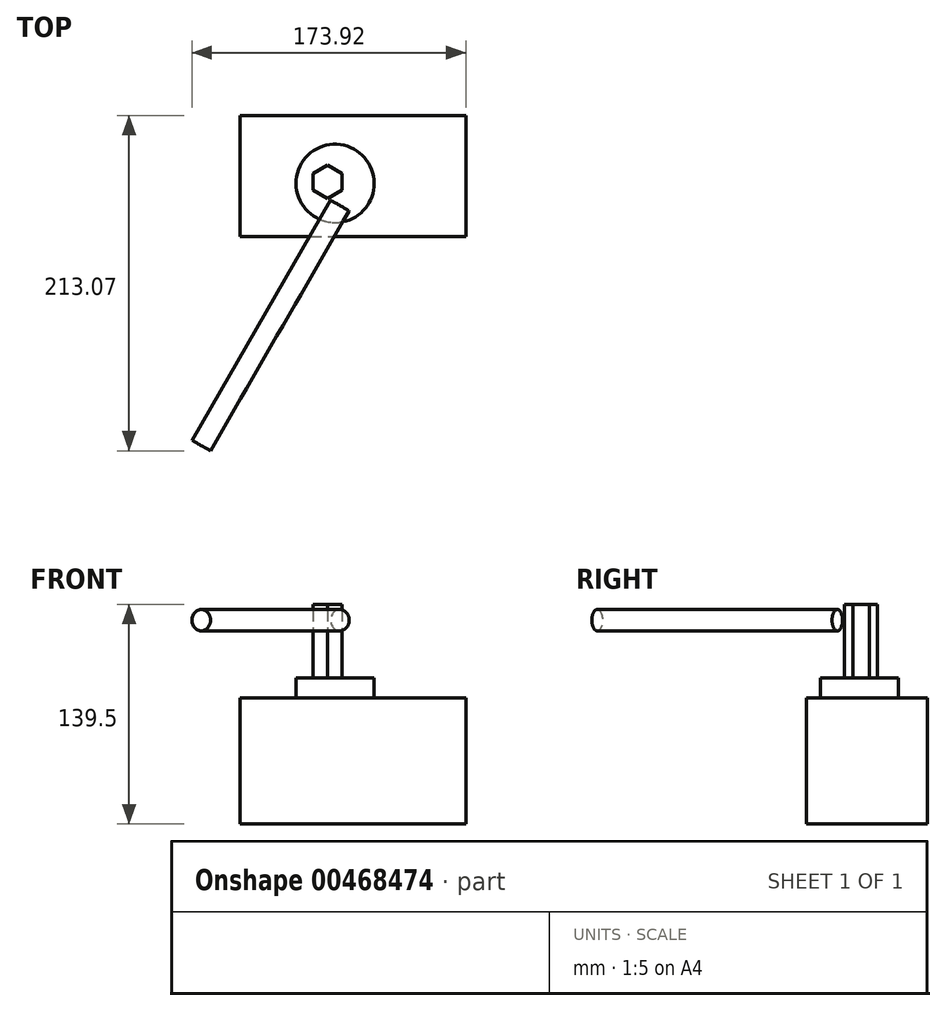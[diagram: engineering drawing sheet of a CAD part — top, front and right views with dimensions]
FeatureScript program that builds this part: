
annotation { "Feature Type Name" : "Feature", "Feature Type Description" : "" }
export const myFeature = defineFeature(function(context is Context, id is Id, definition is map)
    precondition{}
    {
        {
            var Q0;
            Q0=qCreatedBy(makeId("Top.planeOp"),FACE);
            var sketch = newSketch(context, id + "F0", { "sketchPlane" : qUnion([Q0])});
            skLineSegment(sketch, "E0", {"start": v(-105.3, 96.94) * mm, "end": v(109.68, -77.54) * mm});
            skLineSegment(sketch, "E1.bottom", {"start": v(-99.05, 64.2) * mm, "end": v(44.33, 64.2) * mm});
            skLineSegment(sketch, "E1.top", {"start": v(-99.05, -12.7) * mm, "end": v(44.33, -12.7) * mm});
            skLineSegment(sketch, "E1.left", {"start": v(-99.05, 64.2) * mm, "end": v(-99.05, -12.7) * mm});
            skLineSegment(sketch, "E1.right", {"start": v(44.33, 64.2) * mm, "end": v(44.33, -12.7) * mm});
            skSolve(sketch);
        }
        {
            var Q0;
            Q0 = qSketchRegion(id + "F0", true);
            extrude(context, id + "F1", {"entities" : qUnion([Q0]), "depth" : 80.2 * mm});
        }
        {
            var Q0;
            Q0=makeQuery(id+"F1.opExtrude","CAP_FACE",FACE,{"disambiguationData":[OSD([sQuery(id+"F0.wireOp",EDGE,"E1.bottom"),sQuery(id+"F0.wireOp",EDGE,"E1.top"),sQuery(id+"F0.wireOp",EDGE,"E1.left"),sQuery(id+"F0.wireOp",EDGE,"E1.right")])],"isStart":false});
            var sketch = newSketch(context, id + "F2", { "sketchPlane" : qUnion([Q0])});
            skCircle(sketch, "E2", {"center": v(-38.76, 21.04) * mm, "radius": 24.85 * mm});
            skSolve(sketch);
        }
        {
            var Q0;
            Q0=makeQuery(id+"F2.imprint","IMPRINT",FACE,{"disambiguationData":[TD([[makeQuery(id+"F2.imprint","IMPRINT",EDGE,{"derivedFrom":sQuery(id+"F2.wireOp",EDGE,"E2")}),1.0]])]});
            extrude(context, id + "F3", {"entities" : qUnion([Q0]), "operationType" : NewBodyOperationType.ADD, "depth" : 12.7 * mm});
        }
        {
            var Q0;
            Q0=makeQuery(id+"F3.opExtrude","CAP_FACE",FACE,{"disambiguationData":[OSD([sQuery(id+"F2.wireOp",EDGE,"E2")])],"isStart":false});
            var sketch = newSketch(context, id + "F4", { "sketchPlane" : qUnion([Q0])});
            skCircle(sketch, "E3.cCircle", {"center": v(-43.58, 22.07) * mm, "radius": 9.1 * mm, "construction": true});
            skLineSegment(sketch, "E3.0", {"start": v(-34.48, 27.33) * mm, "end": v(-34.48, 16.82) * mm});
            skLineSegment(sketch, "E3.1", {"start": v(-34.48, 16.82) * mm, "end": v(-43.58, 11.56) * mm});
            skLineSegment(sketch, "E3.2", {"start": v(-43.58, 11.56) * mm, "end": v(-52.68, 16.82) * mm});
            skLineSegment(sketch, "E3.3", {"start": v(-52.68, 16.82) * mm, "end": v(-52.68, 27.33) * mm});
            skLineSegment(sketch, "E3.4", {"start": v(-52.68, 27.33) * mm, "end": v(-43.58, 32.58) * mm});
            skLineSegment(sketch, "E3.5", {"start": v(-43.58, 32.58) * mm, "end": v(-34.48, 27.33) * mm});
            skPoint(sketch, "E3.0.midPoint", {"position": v(-34.48, 22.07) * mm});
            skSolve(sketch);
        }
        {
            var Q0;
            Q0 = qSketchRegion(id + "F4", true);
            extrude(context, id + "F5", {"entities" : qUnion([Q0]), "operationType" : NewBodyOperationType.ADD, "depth" : 46.6 * mm});
        }
        {
            var Q0;
            Q0=makeQuery(id+"F5.opExtrude","SWEPT_FACE",FACE,{"disambiguationData":[OSD([sQuery(id+"F4.wireOp",EDGE,"E3.2")])]});
            var sketch = newSketch(context, id + "F6", { "sketchPlane" : qUnion([Q0])});
            skCircle(sketch, "E4", {"center": v(-34.41, 129.5) * mm, "radius": 6.75 * mm});
            skSolve(sketch);
        }
        {
            var Q0;
            Q0 = qSketchRegion(id + "F6", true);
            extrude(context, id + "F7", {"entities" : qUnion([Q0]), "depth" : 176.1 * mm});
        }
    });
